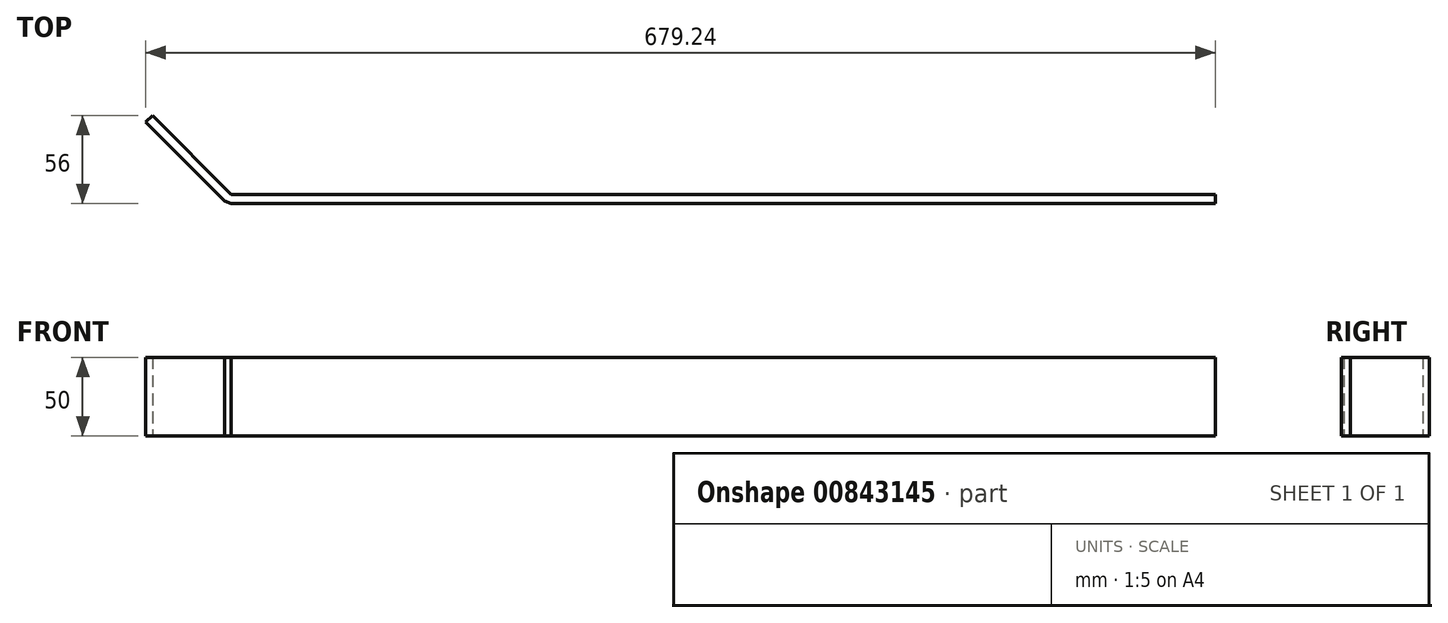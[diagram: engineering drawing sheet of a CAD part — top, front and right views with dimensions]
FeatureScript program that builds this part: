
annotation { "Feature Type Name" : "Feature", "Feature Type Description" : "" }
export const myFeature = defineFeature(function(context is Context, id is Id, definition is map)
    precondition{}
    {
        {
            var Q0;
            Q0=qCreatedBy(makeId("Top.planeOp"),FACE);
            var sketch = newSketch(context, id + "F0", { "sketchPlane" : qUnion([Q0])});
            skLineSegment(sketch, "E0.bottom", {"start": v(312.5, 3) * mm, "end": v(-312.5, 3) * mm});
            skLineSegment(sketch, "E0.top", {"start": v(312.5, -3) * mm, "end": v(-312.5, -3) * mm});
            skLineSegment(sketch, "E0.left", {"start": v(312.5, 3) * mm, "end": v(312.5, -3) * mm});
            skLineSegment(sketch, "E0.right", {"start": v(-312.5, 3) * mm, "end": v(-312.5, -3) * mm});
            skPoint(sketch, "E0.middle", {"position": v(0, 0) * mm});
            skLineSegment(sketch, "E1", {"start": v(-312.5, 3) * mm, "end": v(-312.5, 53) * mm, "construction": true});
            skLineSegment(sketch, "E2", {"start": v(-312.5, 53) * mm, "end": v(-362.5, 53) * mm, "construction": true});
            skLineSegment(sketch, "E3", {"start": v(-312.5, 3) * mm, "end": v(-362.5, 53) * mm});
            skLineSegment(sketch, "E4.0", {"start": v(-316.74, -1.24) * mm, "end": v(-366.74, 48.76) * mm});
            skLineSegment(sketch, "E5", {"start": v(-312.5, -3) * mm, "end": v(-316.74, -1.24) * mm});
            skLineSegment(sketch, "E6", {"start": v(-366.74, 48.76) * mm, "end": v(-362.5, 53) * mm});
            skSolve(sketch);
        }
        {
            var Q0;
            Q0=makeQuery(id+"F0.imprint","IMPRINT",FACE,{"disambiguationData":[TD([[makeQuery(id+"F0.imprint","IMPRINT",EDGE,{"derivedFrom":sQuery(id+"F0.wireOp",EDGE,"E0.bottom")}),1.0]])]});
            var Q1;
            Q1=makeQuery(id+"F0.imprint","IMPRINT",FACE,{"disambiguationData":[TD([[makeQuery(id+"F0.imprint","IMPRINT",EDGE,{"derivedFrom":sQuery(id+"F0.wireOp",EDGE,"E0.right")}),-1.0]])]});
            extrude(context, id + "F1", {"entities" : qUnion([Q0, Q1]), "depth" : 50 * mm, "offsetDistance" : 25 * mm});
        }
    });
